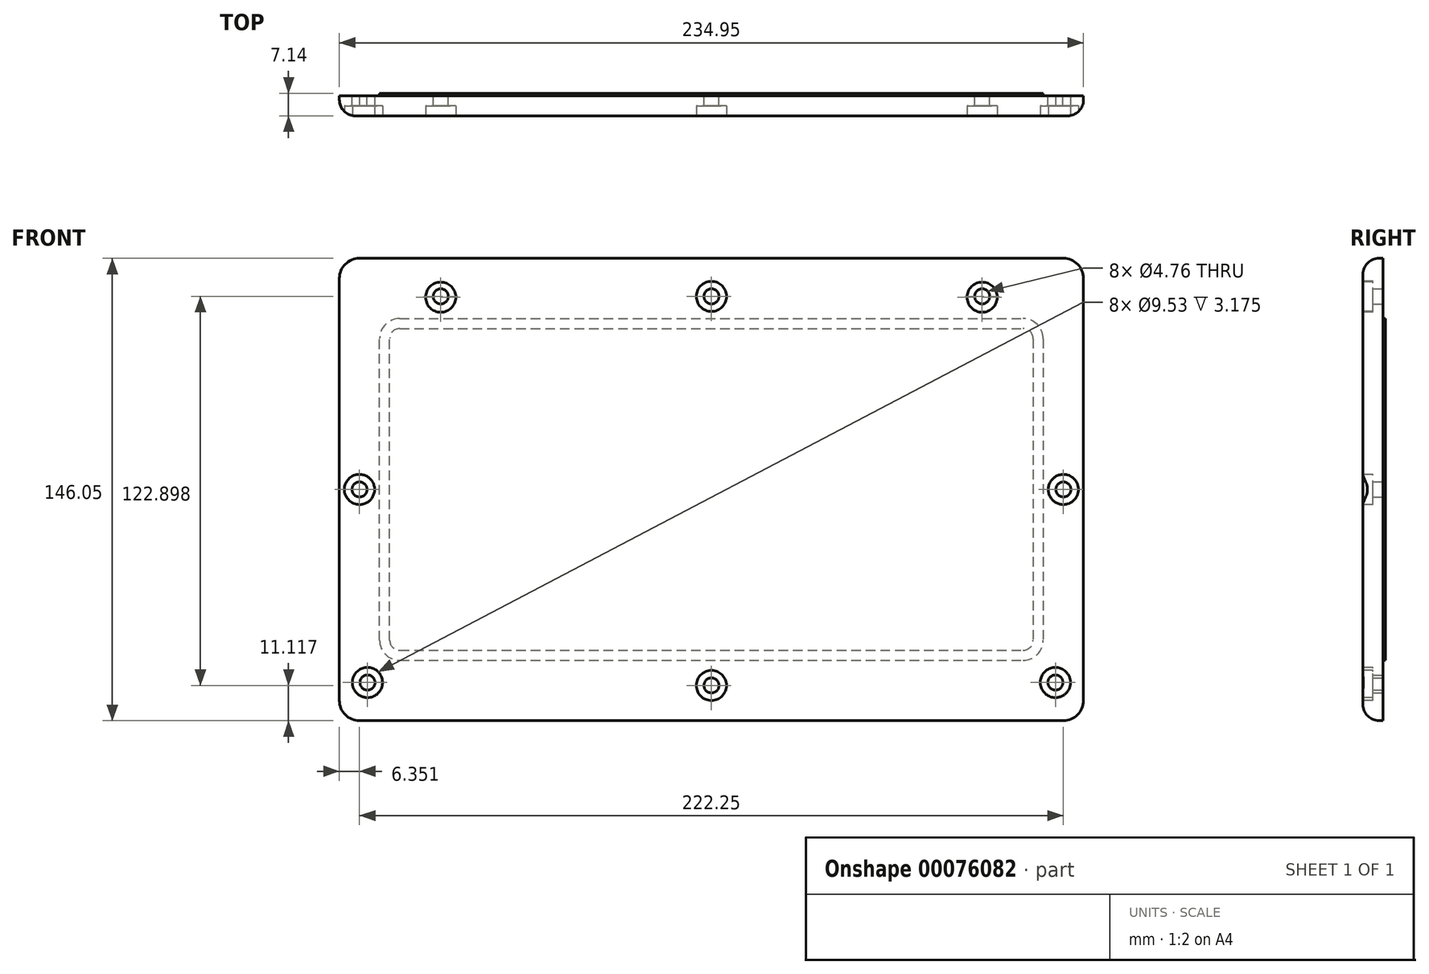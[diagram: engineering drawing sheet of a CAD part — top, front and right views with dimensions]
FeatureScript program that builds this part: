
annotation { "Feature Type Name" : "Feature", "Feature Type Description" : "" }
export const myFeature = defineFeature(function(context is Context, id is Id, definition is map)
    precondition{}
    {
        {
            var Q0;
            Q0=qCreatedBy(makeId("Front.planeOp"),FACE);
            var sketch = newSketch(context, id + "F0", { "sketchPlane" : qUnion([Q0])});
            skPoint(sketch, "E0.visualSharp", {"position": v(-92.06, 54.25) * mm});
            skLineSegment(sketch, "E1.0", {"start": v(-98.4, 73.3) * mm, "end": v(123.84, 73.3) * mm});
            skLineSegment(sketch, "E2.0", {"start": v(-98.4, -72.75) * mm, "end": v(123.84, -72.75) * mm});
            skLineSegment(sketch, "E3.0", {"start": v(-104.76, 66.95) * mm, "end": v(-104.76, -66.4) * mm});
            skLineSegment(sketch, "E4.0", {"start": v(130.2, 66.95) * mm, "end": v(130.2, -66.4) * mm});
            skPoint(sketch, "E5.visualSharp", {"position": v(-104.76, 73.3) * mm});
            skArc(sketch, "E5.filletArc", {"start": v(-98.4, 73.3) * mm, "mid": v(-102.9, 71.44) * mm, "end": v(-104.76, 66.95) * mm});
            skPoint(sketch, "E6.visualSharp", {"position": v(130.2, 73.3) * mm});
            skArc(sketch, "E6.filletArc", {"start": v(130.2, 66.95) * mm, "mid": v(128.33, 71.44) * mm, "end": v(123.84, 73.3) * mm});
            skPoint(sketch, "E7.visualSharp", {"position": v(130.2, -72.75) * mm});
            skArc(sketch, "E7.filletArc", {"start": v(123.84, -72.75) * mm, "mid": v(128.33, -70.89) * mm, "end": v(130.2, -66.4) * mm});
            skPoint(sketch, "E8.visualSharp", {"position": v(-104.76, -72.75) * mm});
            skArc(sketch, "E8.filletArc", {"start": v(-104.76, -66.4) * mm, "mid": v(-102.9, -70.89) * mm, "end": v(-98.4, -72.75) * mm});
            skLineSegment(sketch, "E9", {"start": v(-104.76, 66.95) * mm, "end": v(-98.4, 73.3) * mm, "construction": true});
            skLineSegment(sketch, "E10", {"start": v(-101.58, 70.13) * mm, "end": v(-90.2, 52.4) * mm, "construction": true});
            skLineSegment(sketch, "E11", {"start": v(-104.76, 0.28) * mm, "end": v(-92.06, 0.28) * mm, "construction": true});
            skLineSegment(sketch, "E12", {"start": v(-98.4, -72.75) * mm, "end": v(-104.76, -66.4) * mm, "construction": true});
            skPoint(sketch, "E13.startSnap0", {"position": v(12.72, 73.3) * mm});
            skLineSegment(sketch, "E14", {"start": v(-137.08, 0.28) * mm, "end": v(218.2, 0.28) * mm, "construction": true});
            skLineSegment(sketch, "E15", {"start": v(-85.7, 54.25) * mm, "end": v(-85.7, 73.3) * mm, "construction": true});
            skCircle(sketch, "E16", {"center": v(-98.4, 0.28) * mm, "radius": 2.38 * mm});
            skCircle(sketch, "E17", {"center": v(-95.9, -60.7) * mm, "radius": 2.38 * mm});
            skLineSegment(sketch, "E18", {"start": v(-85.7, -53.7) * mm, "end": v(-85.7, -72.75) * mm, "construction": true});
            skLineSegment(sketch, "E19", {"start": v(-85.7, -72.75) * mm, "end": v(-85.7, -63.22) * mm, "construction": true});
            skLineSegment(sketch, "E20", {"start": v(-85.7, -63.22) * mm, "end": v(52.67, -63.22) * mm, "construction": true});
            skLineSegment(sketch, "E21", {"start": v(12.72, 54.25) * mm, "end": v(12.72, 73.3) * mm, "construction": true});
            skLineSegment(sketch, "E22", {"start": v(12.72, -72.75) * mm, "end": v(12.72, -53.7) * mm, "construction": true});
            skCircle(sketch, "E23", {"center": v(12.72, 61.26) * mm, "radius": 2.38 * mm});
            skCircle(sketch, "E24.MirrorC", {"center": v(123.84, 0.28) * mm, "radius": 2.38 * mm});
            skCircle(sketch, "E25.MirrorC", {"center": v(121.32, -60.7) * mm, "radius": 2.38 * mm});
            skCircle(sketch, "E26.MirrorC", {"center": v(12.72, -61.63) * mm, "radius": 2.38 * mm});
            skLineSegment(sketch, "E27", {"start": v(-90.75, 61.26) * mm, "end": v(119.17, 61.26) * mm, "construction": true});
            skCircle(sketch, "E28", {"center": v(-72.76, 61.26) * mm, "radius": 2.38 * mm});
            skCircle(sketch, "E29", {"center": v(98.2, 61.26) * mm, "radius": 2.38 * mm});
            skSolve(sketch);
        }
        {
            var Q0;
            Q0 = qSketchRegion(id + "F0", true);
            extrude(context, id + "F1", {"entities" : qUnion([Q0]), "depth" : 6.35 * mm});
        }
        {
            var Q0;
            Q0=makeQuery(id+"F1.opExtrude","CAP_FACE",FACE,{"disambiguationData":[OSD([sQuery(id+"F0.wireOp",EDGE,"E1.0"),sQuery(id+"F0.wireOp",EDGE,"E2.0"),sQuery(id+"F0.wireOp",EDGE,"E3.0"),sQuery(id+"F0.wireOp",EDGE,"E4.0"),sQuery(id+"F0.wireOp",EDGE,"E5.filletArc"),sQuery(id+"F0.wireOp",EDGE,"E6.filletArc"),sQuery(id+"F0.wireOp",EDGE,"E7.filletArc"),sQuery(id+"F0.wireOp",EDGE,"E8.filletArc"),sQuery(id+"F0.wireOp",EDGE,"a652ad49-27b8-48a3-b818-1bd37121d45f"),sQuery(id+"F0.wireOp",EDGE,"E16"),sQuery(id+"F0.wireOp",EDGE,"E17"),sQuery(id+"F0.wireOp",EDGE,"E23"),sQuery(id+"F0.wireOp",EDGE,"34debe28-ff95-48b9-a325-31e0bb5e3f18.MirrorC"),sQuery(id+"F0.wireOp",EDGE,"E24.MirrorC"),sQuery(id+"F0.wireOp",EDGE,"E25.MirrorC"),sQuery(id+"F0.wireOp",EDGE,"E26.MirrorC")])],"isStart":false});
            var sketch = newSketch(context, id + "F2", { "sketchPlane" : qUnion([Q0])});
            skCircle(sketch, "E30", {"center": v(12.72, 61.26) * mm, "radius": 4.76 * mm});
            skCircle(sketch, "E31", {"center": v(123.84, 0.28) * mm, "radius": 4.76 * mm});
            skCircle(sketch, "E32", {"center": v(121.32, -60.7) * mm, "radius": 4.76 * mm});
            skCircle(sketch, "E33", {"center": v(12.72, -61.63) * mm, "radius": 4.76 * mm});
            skCircle(sketch, "E34", {"center": v(-95.9, -60.7) * mm, "radius": 4.76 * mm});
            skCircle(sketch, "E35", {"center": v(-98.4, 0.28) * mm, "radius": 4.76 * mm});
            skSolve(sketch);
        }
        {
            var Q0;
            Q0 = qSketchRegion(id + "F2", true);
            extrude(context, id + "F3", {"entities" : qUnion([Q0]), "operationType" : NewBodyOperationType.REMOVE, "oppositeDirection" : true, "depth" : 3.17 * mm});
        }
        {
            var Q0;
            Q0=makeQuery(id+"F1.opExtrude","CAP_EDGE",EDGE,{"disambiguationData":[OSD([sQuery(id+"F0.wireOp",EDGE,"E3.0")])],"isStart":false});
            var Q1;
            Q1=makeQuery(id+"F1.opExtrude","CAP_EDGE",EDGE,{"disambiguationData":[OSD([sQuery(id+"F0.wireOp",EDGE,"E5.filletArc")])],"isStart":false});
            var Q2;
            Q2=makeQuery(id+"F1.opExtrude","CAP_EDGE",EDGE,{"disambiguationData":[OSD([sQuery(id+"F0.wireOp",EDGE,"E1.0")])],"isStart":false});
            fillet(context, id + "F4", {"entities" : qUnion([Q0, Q1, Q2]), "radius" : 5.08 * mm, "tangentPropagation" : true, "allowEdgeOverflow" : false});
        }
        {
            var Q0;
            Q0=makeQuery(id+"F0.imprint","IMPRINT",FACE,{"disambiguationData":[TD([[makeQuery(id+"F0.imprint","IMPRINT",EDGE,{"derivedFrom":sQuery(id+"F0.wireOp",EDGE,"E1.0")}),-1.0]])]});
            var sketch = newSketch(context, id + "F5", { "sketchPlane" : qUnion([Q0])});
            skLineSegment(sketch, "E36.0", {"start": v(-92.06, -47.35) * mm, "end": v(-92.06, 47.9) * mm});
            skLineSegment(sketch, "E37.0", {"start": v(117.5, 47.9) * mm, "end": v(117.5, -47.35) * mm});
            skLineSegment(sketch, "E38", {"start": v(-85.7, 54.25) * mm, "end": v(111.14, 54.25) * mm});
            skLineSegment(sketch, "E39", {"start": v(-85.7, -53.7) * mm, "end": v(111.14, -53.7) * mm});
            skPoint(sketch, "E40.visualSharp", {"position": v(-92.06, 54.25) * mm});
            skArc(sketch, "E40.filletArc", {"start": v(-85.7, 54.25) * mm, "mid": v(-90.2, 52.4) * mm, "end": v(-92.06, 47.9) * mm});
            skPoint(sketch, "E41.visualSharp", {"position": v(-92.06, -53.7) * mm});
            skArc(sketch, "E41.filletArc", {"start": v(-92.06, -47.35) * mm, "mid": v(-90.2, -51.84) * mm, "end": v(-85.7, -53.7) * mm});
            skPoint(sketch, "E42.visualSharp", {"position": v(117.5, -53.7) * mm});
            skArc(sketch, "E42.filletArc", {"start": v(111.14, -53.7) * mm, "mid": v(115.63, -51.84) * mm, "end": v(117.5, -47.35) * mm});
            skPoint(sketch, "E43.visualSharp", {"position": v(117.5, 54.25) * mm});
            skArc(sketch, "E43.filletArc", {"start": v(117.5, 47.9) * mm, "mid": v(115.63, 52.4) * mm, "end": v(111.14, 54.25) * mm});
            skArc(sketch, "E44.0", {"start": v(-85.7, 51.08) * mm, "mid": v(-87.95, 50.15) * mm, "end": v(-88.88, 47.9) * mm});
            skLineSegment(sketch, "E44.1", {"start": v(-88.88, -47.35) * mm, "end": v(-88.88, 47.9) * mm});
            skLineSegment(sketch, "E44.2", {"start": v(-85.7, 51.08) * mm, "end": v(111.14, 51.08) * mm});
            skArc(sketch, "E44.3", {"start": v(-88.88, -47.35) * mm, "mid": v(-87.95, -49.6) * mm, "end": v(-85.7, -50.52) * mm});
            skArc(sketch, "E44.4", {"start": v(114.32, 47.9) * mm, "mid": v(113.39, 50.15) * mm, "end": v(111.14, 51.08) * mm});
            skLineSegment(sketch, "E44.5", {"start": v(114.32, 47.9) * mm, "end": v(114.32, -47.35) * mm});
            skArc(sketch, "E44.6", {"start": v(111.14, -50.52) * mm, "mid": v(113.39, -49.6) * mm, "end": v(114.32, -47.35) * mm});
            skLineSegment(sketch, "E44.7", {"start": v(-85.7, -50.52) * mm, "end": v(111.14, -50.52) * mm});
            skSolve(sketch);
        }
        {
            var Q0;
            Q0 = qSketchRegion(id + "F5", true);
            extrude(context, id + "F6", {"entities" : qUnion([Q0]), "operationType" : NewBodyOperationType.ADD, "oppositeDirection" : true, "depth" : 0.8 * mm});
        }
        {
            var Q0;
            Q0=makeQuery(id+"F1.opExtrude","CAP_FACE",FACE,{"disambiguationData":[OSD([sQuery(id+"F0.wireOp",EDGE,"E1.0"),sQuery(id+"F0.wireOp",EDGE,"E2.0"),sQuery(id+"F0.wireOp",EDGE,"E3.0"),sQuery(id+"F0.wireOp",EDGE,"E4.0"),sQuery(id+"F0.wireOp",EDGE,"E5.filletArc"),sQuery(id+"F0.wireOp",EDGE,"E6.filletArc"),sQuery(id+"F0.wireOp",EDGE,"E7.filletArc"),sQuery(id+"F0.wireOp",EDGE,"E8.filletArc"),sQuery(id+"F0.wireOp",EDGE,"E16"),sQuery(id+"F0.wireOp",EDGE,"E17"),sQuery(id+"F0.wireOp",EDGE,"E23"),sQuery(id+"F0.wireOp",EDGE,"E24.MirrorC"),sQuery(id+"F0.wireOp",EDGE,"E25.MirrorC"),sQuery(id+"F0.wireOp",EDGE,"E26.MirrorC")])],"isStart":false});
            var sketch = newSketch(context, id + "F7", { "sketchPlane" : qUnion([Q0])});
            skCircle(sketch, "E45", {"center": v(-72.76, 61.02) * mm, "radius": 2.38 * mm});
            skLineSegment(sketch, "E46", {"start": v(12.72, -72.4) * mm, "end": v(12.72, 73.86) * mm, "construction": true});
            skPoint(sketch, "E46.startSnap0", {"position": v(12.72, -67.67) * mm});
            skLineSegment(sketch, "E47", {"start": v(-104.74, 0) * mm, "end": v(130.66, 0.28) * mm, "construction": true});
            skPoint(sketch, "E47.endSnap0", {"position": v(-93.65, 0.28) * mm});
            skCircle(sketch, "E48.MirrorC", {"center": v(98.2, 61.02) * mm, "radius": 2.38 * mm});
            skSolve(sketch);
        }
        {
            var Q0;
            Q0=makeQuery(id+"F7.imprint","IMPRINT",FACE,{"disambiguationData":[TD([[makeQuery(id+"F7.imprint","IMPRINT",EDGE,{"derivedFrom":sQuery(id+"F7.wireOp",EDGE,"E45")}),1.0]])]});
            var sketch = newSketch(context, id + "F8", { "sketchPlane" : qUnion([Q0])});
            skCircle(sketch, "E49", {"center": v(-72.76, 61.02) * mm, "radius": 4.76 * mm});
            skCircle(sketch, "E50", {"center": v(98.2, 61.02) * mm, "radius": 4.76 * mm});
            skSolve(sketch);
        }
        {
            var Q0;
            Q0 = qSketchRegion(id + "F8", true);
            extrude(context, id + "F9", {"entities" : qUnion([Q0]), "operationType" : NewBodyOperationType.REMOVE, "oppositeDirection" : true, "depth" : 3.17 * mm});
        }
    });
